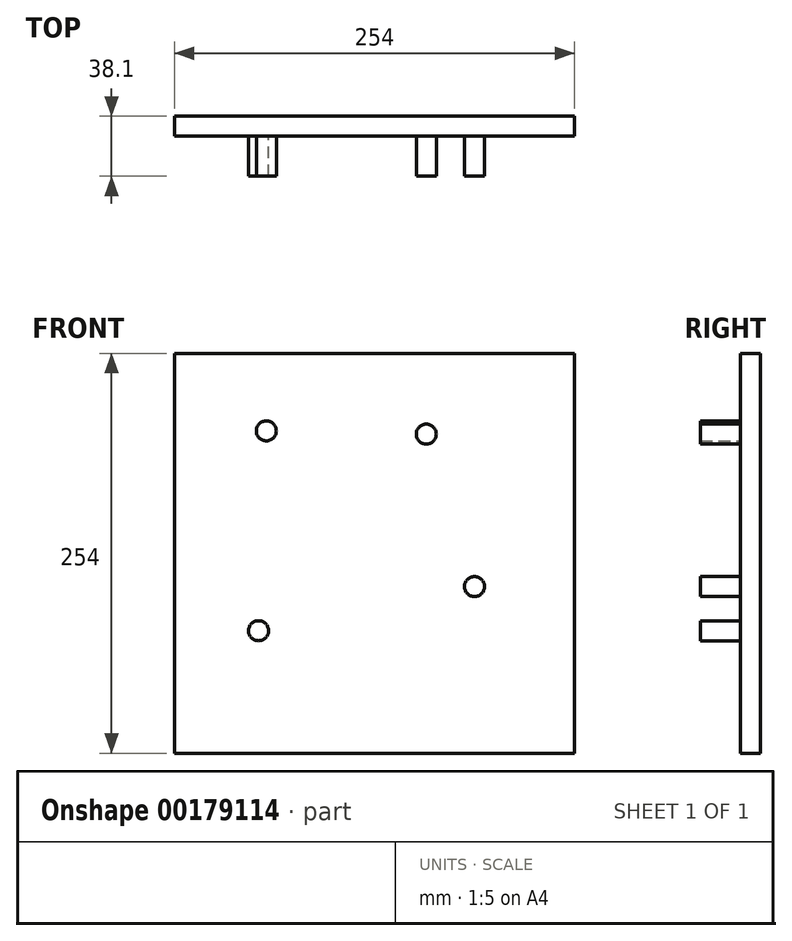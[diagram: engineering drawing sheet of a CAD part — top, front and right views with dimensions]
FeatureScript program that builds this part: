
annotation { "Feature Type Name" : "Feature", "Feature Type Description" : "" }
export const myFeature = defineFeature(function(context is Context, id is Id, definition is map)
    precondition{}
    {
        {
            var Q0;
            Q0=qCreatedBy(makeId("Front.planeOp"),FACE);
            var sketch = newSketch(context, id + "F0", { "sketchPlane" : qUnion([Q0])});
            skLineSegment(sketch, "E0.bottom", {"start": v(-127, 127) * mm, "end": v(127, 127) * mm});
            skLineSegment(sketch, "E0.top", {"start": v(-127, -127) * mm, "end": v(127, -127) * mm});
            skLineSegment(sketch, "E0.left", {"start": v(-127, 127) * mm, "end": v(-127, -127) * mm});
            skLineSegment(sketch, "E0.right", {"start": v(127, 127) * mm, "end": v(127, -127) * mm});
            skSolve(sketch);
        }
        {
            var Q0;
            Q0 = qSketchRegion(id + "F0", true);
            extrude(context, id + "F1", {"entities" : qUnion([Q0]), "depth" : 12.7 * mm});
        }
        {
            var Q0;
            Q0=makeQuery(id+"F1.opExtrude","CAP_FACE",FACE,{"disambiguationData":[OSD([sQuery(id+"F0.wireOp",EDGE,"E0.bottom"),sQuery(id+"F0.wireOp",EDGE,"E0.top"),sQuery(id+"F0.wireOp",EDGE,"E0.left"),sQuery(id+"F0.wireOp",EDGE,"E0.right")])],"isStart":false});
            var sketch = newSketch(context, id + "F2", { "sketchPlane" : qUnion([Q0])});
            skCircle(sketch, "E1", {"center": v(-73.66, -49.18) * mm, "radius": 6.35 * mm});
            skCircle(sketch, "E2", {"center": v(-68.72, 77.72) * mm, "radius": 6.35 * mm});
            skCircle(sketch, "E3", {"center": v(32.86, 75.7) * mm, "radius": 6.35 * mm});
            skCircle(sketch, "E4", {"center": v(63.5, -21.17) * mm, "radius": 6.35 * mm});
            skLineSegment(sketch, "E5", {"start": v(-68.72, 77.72) * mm, "end": v(-73.66, -49.18) * mm});
            skLineSegment(sketch, "E6", {"start": v(-68.72, 77.72) * mm, "end": v(32.86, 75.7) * mm});
            skLineSegment(sketch, "E7", {"start": v(63.5, -21.17) * mm, "end": v(32.86, 75.7) * mm});
            skSolve(sketch);
        }
        {
            var Q0;
            {var subQ0=sQuery(id+"F2.wireOp",EDGE,"E5");var subQ1=sQuery(id+"F2.wireOp",EDGE,"E2");var subQ2=makeQuery(id+"F2.imprint","INTERSECT",VERTEX,{"derivedFrom":[subQ1,subQ0]});Q0=makeQuery(id+"F2.imprint","IMPRINT",FACE,{"disambiguationData":[TD([[makeQuery(id+"F2.imprint","IMPRINT",EDGE,{"disambiguationData":[TD([[subQ2,1.0]])],"derivedFrom":subQ1}),1.0]])]});}
            var Q1;
            {var subQ0=sQuery(id+"F2.wireOp",EDGE,"E5");var subQ1=sQuery(id+"F2.wireOp",EDGE,"E2");var subQ2=makeQuery(id+"F2.imprint","INTERSECT",VERTEX,{"derivedFrom":[subQ1,subQ0]});Q1=makeQuery(id+"F2.imprint","IMPRINT",FACE,{"disambiguationData":[TD([[makeQuery(id+"F2.imprint","IMPRINT",EDGE,{"disambiguationData":[TD([[subQ2,-1.0]])],"derivedFrom":subQ1}),1.0]])]});}
            var Q2;
            {var subQ0=sQuery(id+"F2.wireOp",EDGE,"E6");var subQ1=sQuery(id+"F2.wireOp",EDGE,"E3");var subQ2=makeQuery(id+"F2.imprint","INTERSECT",VERTEX,{"derivedFrom":[subQ1,subQ0]});Q2=makeQuery(id+"F2.imprint","IMPRINT",FACE,{"disambiguationData":[TD([[makeQuery(id+"F2.imprint","IMPRINT",EDGE,{"disambiguationData":[TD([[subQ2,1.0]])],"derivedFrom":subQ1}),1.0]])]});}
            var Q3;
            {var subQ0=sQuery(id+"F2.wireOp",EDGE,"E6");var subQ1=sQuery(id+"F2.wireOp",EDGE,"E3");var subQ2=makeQuery(id+"F2.imprint","INTERSECT",VERTEX,{"derivedFrom":[subQ1,subQ0]});Q3=makeQuery(id+"F2.imprint","IMPRINT",FACE,{"disambiguationData":[TD([[makeQuery(id+"F2.imprint","IMPRINT",EDGE,{"disambiguationData":[TD([[subQ2,-1.0]])],"derivedFrom":subQ1}),1.0]])]});}
            var Q4;
            Q4=makeQuery(id+"F2.imprint","IMPRINT",FACE,{"disambiguationData":[TD([[makeQuery(id+"F2.imprint","IMPRINT",EDGE,{"derivedFrom":sQuery(id+"F2.wireOp",EDGE,"E4")}),1.0]])]});
            var Q5;
            Q5=makeQuery(id+"F2.imprint","IMPRINT",FACE,{"disambiguationData":[TD([[makeQuery(id+"F2.imprint","IMPRINT",EDGE,{"derivedFrom":sQuery(id+"F2.wireOp",EDGE,"E1")}),1.0]])]});
            extrude(context, id + "F3", {"entities" : qUnion([Q0, Q1, Q2, Q3, Q4, Q5]), "operationType" : NewBodyOperationType.ADD, "depth" : 25.4 * mm});
        }
    });
